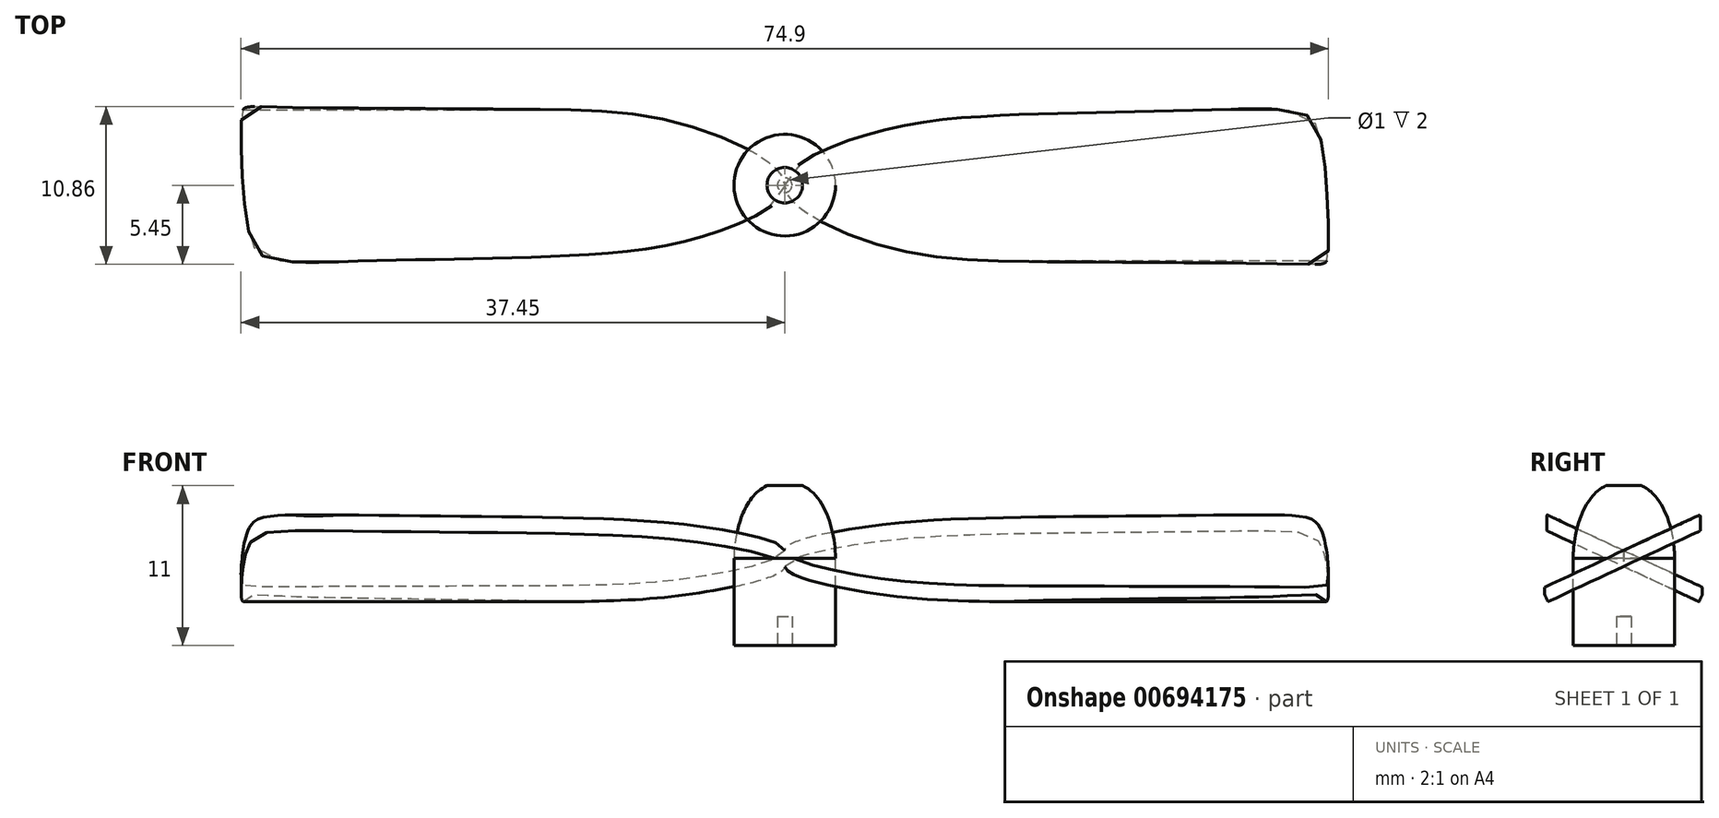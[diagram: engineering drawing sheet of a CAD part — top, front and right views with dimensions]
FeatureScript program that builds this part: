
annotation { "Feature Type Name" : "Feature", "Feature Type Description" : "" }
export const myFeature = defineFeature(function(context is Context, id is Id, definition is map)
    precondition{}
    {
        {
            var Q0;
            Q0=qCreatedBy(makeId("Right.planeOp"),FACE);
            var sketch = newSketch(context, id + "F0", { "sketchPlane" : qUnion([Q0])});
            skLineSegment(sketch, "E0", {"start": v(-5.65, 3.92) * mm, "end": v(5.23, 8.99) * mm});
            skLineSegment(sketch, "E1", {"start": v(5.23, 8.99) * mm, "end": v(5.65, 8.08) * mm});
            skLineSegment(sketch, "E2", {"start": v(5.65, 8.08) * mm, "end": v(-5.23, 3.01) * mm});
            skLineSegment(sketch, "E3", {"start": v(-5.23, 3.01) * mm, "end": v(-5.65, 3.92) * mm});
            skLineSegment(sketch, "E4", {"start": v(0, 0) * mm, "end": v(0, 6) * mm, "construction": true});
            skLineSegment(sketch, "E5", {"start": v(-5.23, 3.01) * mm, "end": v(-5.23, -13.05) * mm, "construction": true});
            skLineSegment(sketch, "E6", {"start": v(-5.23, -13.05) * mm, "end": v(5.23, -13.05) * mm, "construction": true});
            skLineSegment(sketch, "E7", {"start": v(-0.21, 6.45) * mm, "end": v(0.21, 5.55) * mm});
            skLineSegment(sketch, "E8", {"start": v(5.23, -13.05) * mm, "end": v(5.23, 8.99) * mm, "construction": true});
            skSolve(sketch);
        }
        {
            var Q0;
            Q0=qSketchRegion(id+"F0",true);
            extrude(context, id + "F1", {"entities" : qUnion([Q0]), "depth" : 37.5 * mm, "offsetDistance" : 25.4 * mm});
        }
        {
            var Q0;
            Q0=qCreatedBy(makeId("Top.planeOp"),FACE);
            var sketch = newSketch(context, id + "F2", { "sketchPlane" : qUnion([Q0])});
            skFitSpline(sketch, "E9", {"points": [v(0, 0) * mm, v(5.55, 3.45) * mm, v(13.82, 4.75) * mm, v(22.26, 5.03) * mm, v(29.42, 5.19) * mm, v(35.5, 5.02) * mm, v(36.5, 4.28) * mm, v(37.16, 1.66) * mm, v(37.39, -4.93) * mm, v(37.16, -5.37) * mm, v(35.24, -5.43) * mm, v(17.67, -5.27) * mm, v(6.12, -4) * mm, v(0, 0) * mm]});
            skLineSegment(sketch, "E10.bottom", {"start": v(43.66, 21.32) * mm, "end": v(-43.66, 21.32) * mm});
            skLineSegment(sketch, "E10.top", {"start": v(43.66, -21.32) * mm, "end": v(-43.66, -21.32) * mm});
            skLineSegment(sketch, "E10.left", {"start": v(43.66, 21.32) * mm, "end": v(43.66, -21.32) * mm});
            skLineSegment(sketch, "E10.right", {"start": v(-43.66, 21.32) * mm, "end": v(-43.66, -21.32) * mm});
            skSolve(sketch);
        }
        {
            var Q0;
            Q0=qSketchRegion(id+"F2",true);
            extrude(context, id + "F3", {"entities" : qUnion([Q0]), "operationType" : NewBodyOperationType.REMOVE, "depth" : 20 * mm, "offsetDistance" : 25.4 * mm});
        }
        {
            var Q0;
            Q0=makeQuery(id+"F1.opExtrude","SWEPT_BODY",BODY,{"disambiguationData":[OSD([sQuery(id+"F0.wireOp",EDGE,"E0"),sQuery(id+"F0.wireOp",EDGE,"E1"),sQuery(id+"F0.wireOp",EDGE,"E2"),sQuery(id+"F0.wireOp",EDGE,"E3")])]});
            var Q1;
            Q1=makeQuery(id+"F3.boolean.opBoolean","INTERSECT",EDGE,{"disambiguationData":[OD(0.0)],"derivedFrom":[makeQuery(id+"F1.opExtrude","CAP_FACE",FACE,{"disambiguationData":[OSD([sQuery(id+"F0.wireOp",EDGE,"E0"),sQuery(id+"F0.wireOp",EDGE,"E1"),sQuery(id+"F0.wireOp",EDGE,"E2"),sQuery(id+"F0.wireOp",EDGE,"E3")])],"isStart":true}),makeQuery(id+"F3.opExtrude","SWEPT_FACE",FACE,{"disambiguationData":[OSD([sQuery(id+"F2.wireOp",EDGE,"E9")])]})]});
            circularPattern(context, id + "F4", {"entities" : qUnion([Q0]), "axis" : qUnion([Q1]), "angle" : 360 * degree, "instanceCount" : 2, "equalSpace" : true});
        }
        {
            var Q0;
            Q0=qCreatedBy(makeId("Front.planeOp"),FACE);
            var sketch = newSketch(context, id + "F5", { "sketchPlane" : qUnion([Q0])});
            skLineSegment(sketch, "E11", {"start": v(0, 0) * mm, "end": v(-3.5, 0) * mm});
            skLineSegment(sketch, "E12", {"start": v(-3.5, 0) * mm, "end": v(-3.5, 6) * mm});
            skFitSpline(sketch, "E13", {"points": [v(-3.5, 6) * mm, v(-1.22, 11) * mm], "startDerivative": vector(0.09, 5.63) * mm, "endDerivative": vector(4.68, 2.03) * mm});
            skLineSegment(sketch, "E14", {"start": v(-1.22, 11) * mm, "end": v(0, 11) * mm});
            skLineSegment(sketch, "E15", {"start": v(0, 11) * mm, "end": v(0, 0) * mm});
            skSolve(sketch);
        }
        {
            var Q0;
            Q0=makeQuery(id+"F5.imprint","IMPRINT",FACE,{"disambiguationData":[TD([[makeQuery(id+"F5.imprint","IMPRINT",EDGE,{"derivedFrom":sQuery(id+"F5.wireOp",EDGE,"E11")}),-1.0]])]});
            var Q1;
            Q1=sQuery(id+"F5.wireOp",EDGE,"E15");
            revolve(context, id + "F6", {"entities" : qUnion([Q0]), "axis" : qUnion([Q1]), "revolveType" : RevolveType.FULL});
        }
        {
            var Q0;
            Q0=makeQuery(id+"F6.opRevolve","SWEPT_FACE",FACE,{"disambiguationData":[OSD([sQuery(id+"F5.wireOp",EDGE,"E11")])]});
            var sketch = newSketch(context, id + "F7", { "sketchPlane" : qUnion([Q0])});
            skCircle(sketch, "E16", {"center": v(0, 0) * mm, "radius": 0.5 * mm});
            skSolve(sketch);
        }
        {
            var Q0;
            Q0=qSketchRegion(id+"F7",true);
            extrude(context, id + "F8", {"entities" : qUnion([Q0]), "operationType" : NewBodyOperationType.REMOVE, "oppositeDirection" : true, "depth" : 2 * mm, "offsetDistance" : 25.4 * mm});
        }
    });
